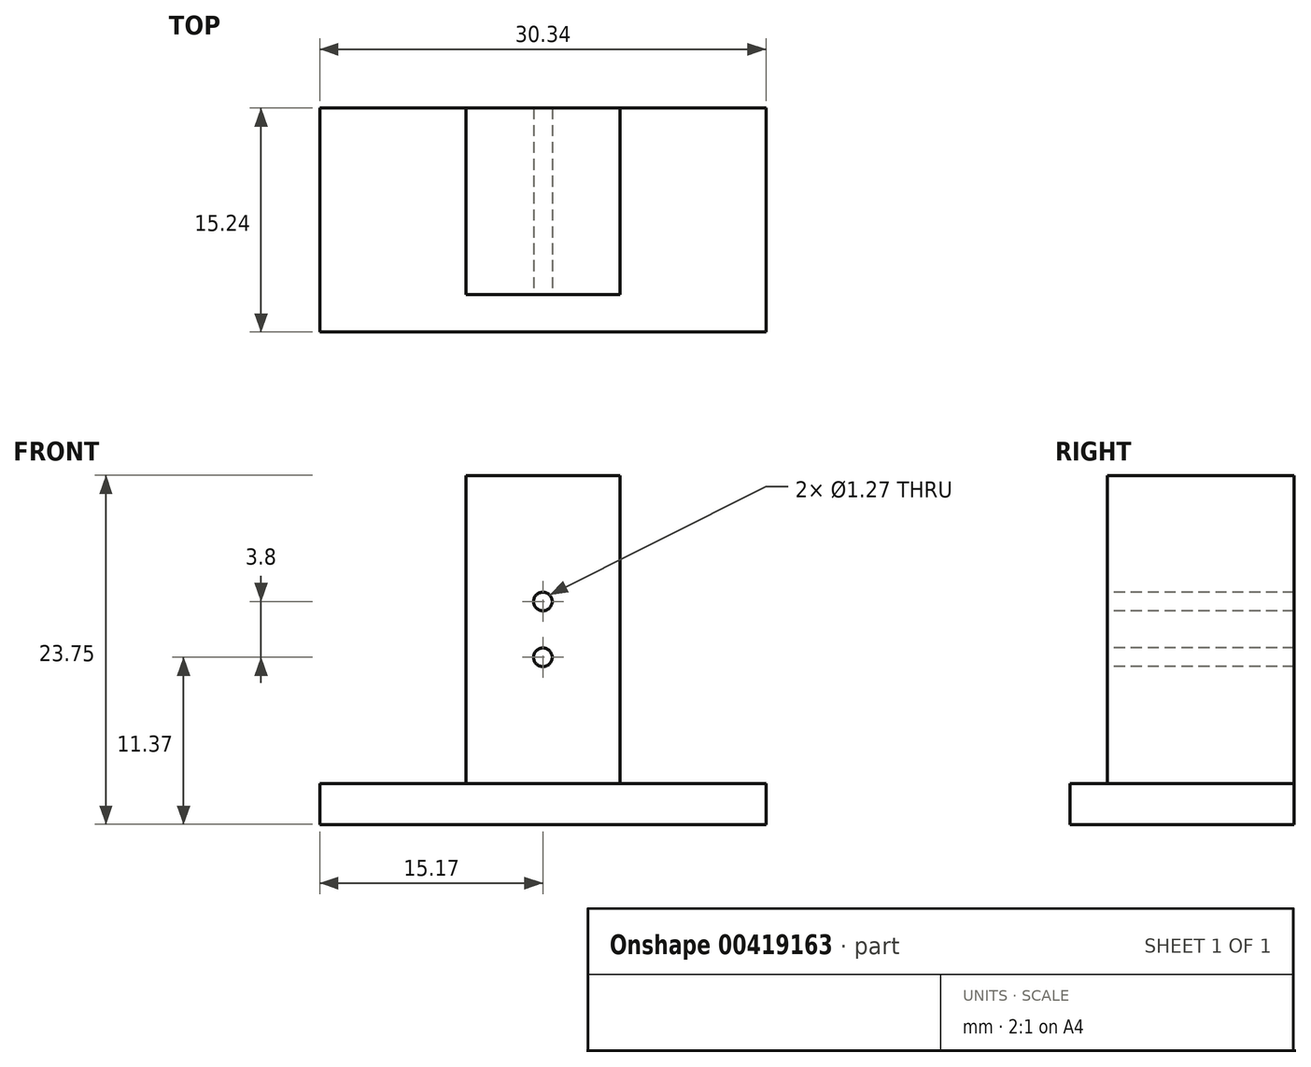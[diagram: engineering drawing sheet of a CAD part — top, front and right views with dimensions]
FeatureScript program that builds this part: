
annotation { "Feature Type Name" : "Feature", "Feature Type Description" : "" }
export const myFeature = defineFeature(function(context is Context, id is Id, definition is map)
    precondition{}
    {
        {
            var Q0;
            Q0=qCreatedBy(makeId("Front.planeOp"),FACE);
            var sketch = newSketch(context, id + "F0", { "sketchPlane" : qUnion([Q0])});
            skLineSegment(sketch, "E0.bottom", {"start": v(-5.24, 10.48) * mm, "end": v(5.24, 10.48) * mm});
            skLineSegment(sketch, "E0.top", {"start": v(-5.24, -10.48) * mm, "end": v(5.24, -10.48) * mm});
            skLineSegment(sketch, "E0.left", {"start": v(-5.24, 10.48) * mm, "end": v(-5.24, -10.48) * mm});
            skLineSegment(sketch, "E0.right", {"start": v(5.24, 10.48) * mm, "end": v(5.24, -10.48) * mm});
            skSolve(sketch);
        }
        {
            var Q0;
            Q0 = qSketchRegion(id + "F0", true);
            extrude(context, id + "F1", {"entities" : qUnion([Q0]), "depth" : 12.7 * mm});
        }
        {
            var Q0;
            Q0=makeQuery(id+"F1.opExtrude","CAP_FACE",FACE,{"disambiguationData":[OSD([sQuery(id+"F0.wireOp",EDGE,"E0.bottom"),sQuery(id+"F0.wireOp",EDGE,"E0.top"),sQuery(id+"F0.wireOp",EDGE,"E0.left"),sQuery(id+"F0.wireOp",EDGE,"E0.right")])],"isStart":false});
            var sketch = newSketch(context, id + "F2", { "sketchPlane" : qUnion([Q0])});
            skCircle(sketch, "E1", {"center": v(0, 1.9) * mm, "radius": 0.25 * mm});
            skCircle(sketch, "E2", {"center": v(0, -1.9) * mm, "radius": 0.25 * mm});
            skSolve(sketch);
        }
        {
            var Q0;
            Q0=qCreatedBy(makeId("Front.planeOp"),FACE);
            var sketch = newSketch(context, id + "F3", { "sketchPlane" : qUnion([Q0])});
            skLineSegment(sketch, "E3.bottom", {"start": v(-15.17, -10.48) * mm, "end": v(15.17, -10.48) * mm});
            skLineSegment(sketch, "E3.top", {"start": v(-15.17, -13.27) * mm, "end": v(15.17, -13.27) * mm});
            skLineSegment(sketch, "E3.left", {"start": v(-15.17, -10.48) * mm, "end": v(-15.17, -13.27) * mm});
            skLineSegment(sketch, "E3.right", {"start": v(15.17, -10.48) * mm, "end": v(15.17, -13.27) * mm});
            skSolve(sketch);
        }
        {
            var Q0;
            Q0=makeQuery(id+"F3.imprint","IMPRINT",FACE,{"disambiguationData":[TD([[makeQuery(id+"F3.imprint","IMPRINT",EDGE,{"derivedFrom":sQuery(id+"F3.wireOp",EDGE,"E3.bottom")}),-1.0]])]});
            extrude(context, id + "F4", {"entities" : qUnion([Q0]), "flatOperationType" : FlatOperationType.REMOVE, "offsetDistance" : 25.4 * mm, "depth" : 15.24 * mm, "domain" : OperationDomain.MODEL});
        }
        {
            var Q0;
            Q0=sQuery(id+"F2.wireOp",VERTEX,"E2.center");
            var Q1;
            Q1=sQuery(id+"F2.wireOp",VERTEX,"E1.center");
            var Q2;
            Q2=makeQuery(id+"F1.opExtrude","SWEPT_BODY",BODY,{"disambiguationData":[OSD([sQuery(id+"F0.wireOp",EDGE,"E0.bottom"),sQuery(id+"F0.wireOp",EDGE,"E0.top"),sQuery(id+"F0.wireOp",EDGE,"E0.left"),sQuery(id+"F0.wireOp",EDGE,"E0.right")])]});
            hole(context, id + "F5", {"style" : HoleStyle.SIMPLE, "endStyle" : HoleEndStyle.THROUGH, "holeDiameter" : 1.27 * mm, "isTappedThrough" : true, "tappedDepth" : 12.7 * mm, "tapClearance" : 3, "locations" : qUnion([Q0, Q1]), "scope" : qUnion([Q2])});
        }
    });
